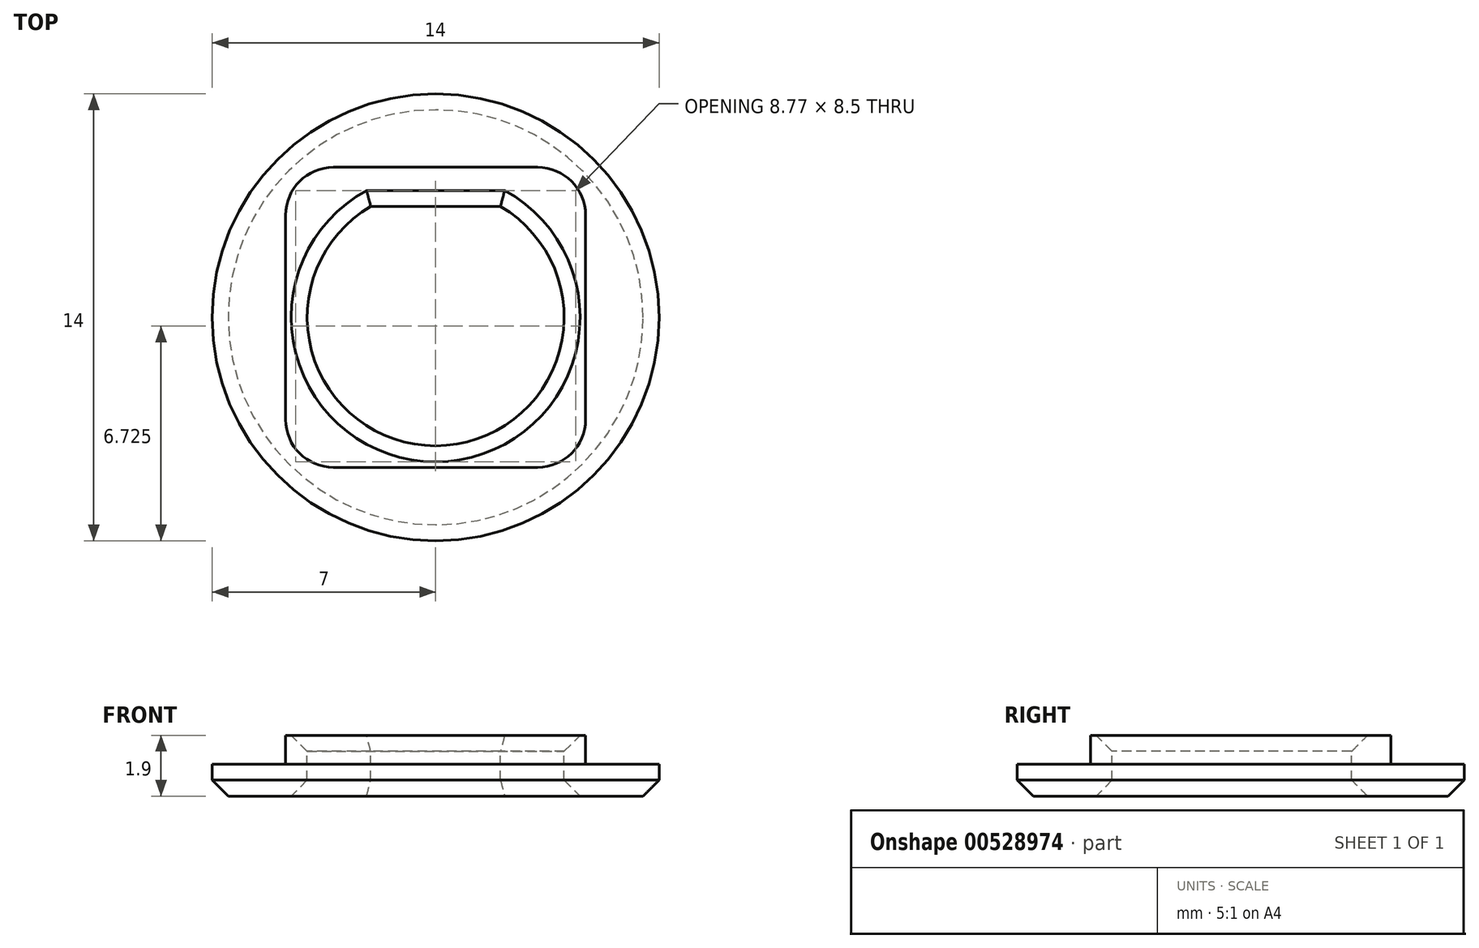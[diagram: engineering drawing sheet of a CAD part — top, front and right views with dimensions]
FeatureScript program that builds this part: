
annotation { "Feature Type Name" : "Feature", "Feature Type Description" : "" }
export const myFeature = defineFeature(function(context is Context, id is Id, definition is map)
    precondition{}
    {
        {
            var Q0;
            Q0=qCreatedBy(makeId("Top.planeOp"),FACE);
            var sketch = newSketch(context, id + "F0", { "sketchPlane" : qUnion([Q0])});
            skCircle(sketch, "E0", {"center": v(0, 0) * mm, "radius": 7 * mm});
            skArc(sketch, "E1", {"start": v(-2.03, 3.47) * mm, "mid": v(0, -4.03) * mm, "end": v(2.03, 3.47) * mm});
            skLineSegment(sketch, "E2", {"start": v(-2.03, 3.47) * mm, "end": v(2.03, 3.47) * mm});
            skSolve(sketch);
        }
        {
            var Q0;
            Q0=makeQuery(id+"F0.imprint","IMPRINT",FACE,{"disambiguationData":[TD([[makeQuery(id+"F0.imprint","IMPRINT",EDGE,{"derivedFrom":sQuery(id+"F0.wireOp",EDGE,"E0")}),1.0]])]});
            extrude(context, id + "F1", {"entities" : qUnion([Q0]), "oppositeDirection" : true, "depth" : 1 * mm, "offsetDistance" : 25 * mm});
        }
        {
            var Q0;
            Q0=makeQuery(id+"F1.opExtrude","CAP_FACE",FACE,{"disambiguationData":[OSD([sQuery(id+"F0.wireOp",EDGE,"E0"),sQuery(id+"F0.wireOp",EDGE,"E1")])],"isStart":true});
            var sketch = newSketch(context, id + "F2", { "sketchPlane" : qUnion([Q0])});
            skLineSegment(sketch, "E3.bottom", {"start": v(-4.7, -4.7) * mm, "end": v(4.7, -4.7) * mm});
            skLineSegment(sketch, "E3.top", {"start": v(-4.7, 4.7) * mm, "end": v(4.7, 4.7) * mm});
            skLineSegment(sketch, "E3.left", {"start": v(-4.7, -4.7) * mm, "end": v(-4.7, 4.7) * mm});
            skLineSegment(sketch, "E3.right", {"start": v(4.7, -4.7) * mm, "end": v(4.7, 4.7) * mm});
            skSolve(sketch);
        }
        {
            var Q0;
            Q0=makeQuery(id+"F2.imprint","IMPRINT",FACE,{"disambiguationData":[TD([[makeQuery(id+"F2.imprint","IMPRINT",EDGE,{"derivedFrom":sQuery(id+"F2.wireOp",EDGE,"E3.bottom")}),1.0]])]});
            extrude(context, id + "F3", {"entities" : qUnion([Q0]), "operationType" : NewBodyOperationType.ADD, "depth" : 0.9 * mm, "offsetDistance" : 25 * mm});
        }
        {
            var Q0;
            Q0=makeQuery(id+"F1.opExtrude","CAP_EDGE",EDGE,{"disambiguationData":[OSD([sQuery(id+"F0.wireOp",EDGE,"E1")])],"isStart":false});
            var Q1;
            Q1=makeQuery(id+"F1.opExtrude","CAP_EDGE",EDGE,{"disambiguationData":[OSD([sQuery(id+"F0.wireOp",EDGE,"E0")])],"isStart":false});
            var Q2;
            Q2=makeQuery(id+"F1.opExtrude","CAP_EDGE",EDGE,{"disambiguationData":[OSD([sQuery(id+"F0.wireOp",EDGE,"E2")])],"isStart":false});
            var Q3;
            Q3=makeQuery(id+"F3.opExtrude","CAP_EDGE",EDGE,{"disambiguationData":[OSD([sQuery(id+"F0.wireOp",EDGE,"E1")])],"isStart":false});
            var Q4;
            Q4=makeQuery(id+"F3.opExtrude","CAP_EDGE",EDGE,{"disambiguationData":[OSD([sQuery(id+"F0.wireOp",EDGE,"E2")])],"isStart":false});
            chamfer(context, id + "F4", {"entities" : qUnion([Q0, Q1, Q2, Q3, Q4]), "chamferType" : ChamferType.OFFSET_ANGLE, "width" : 0.5 * mm, "oppositeDirection" : false, "angle" : 45 * degree, "tangentPropagation" : true});
        }
        {
            var Q0;
            Q0=makeQuery(id+"F3.opExtrude","SWEPT_EDGE",EDGE,{"disambiguationData":[OSD([sQuery(id+"F2.wireOp",EDGE,"E3.top"),sQuery(id+"F2.wireOp",EDGE,"E3.left")])]});
            var Q1;
            Q1=makeQuery(id+"F3.opExtrude","SWEPT_EDGE",EDGE,{"disambiguationData":[OSD([sQuery(id+"F2.wireOp",EDGE,"E3.top"),sQuery(id+"F2.wireOp",EDGE,"E3.right")])]});
            var Q2;
            Q2=makeQuery(id+"F3.opExtrude","SWEPT_EDGE",EDGE,{"disambiguationData":[OSD([sQuery(id+"F2.wireOp",EDGE,"E3.bottom"),sQuery(id+"F2.wireOp",EDGE,"E3.right")])]});
            var Q3;
            Q3=makeQuery(id+"F3.opExtrude","SWEPT_EDGE",EDGE,{"disambiguationData":[OSD([sQuery(id+"F2.wireOp",EDGE,"E3.bottom"),sQuery(id+"F2.wireOp",EDGE,"E3.left")])]});
            fillet(context, id + "F5", {"entities" : qUnion([Q0, Q1, Q2, Q3]), "radius" : 1.5 * mm, "tangentPropagation" : true, "allowEdgeOverflow" : false});
        }
    });
